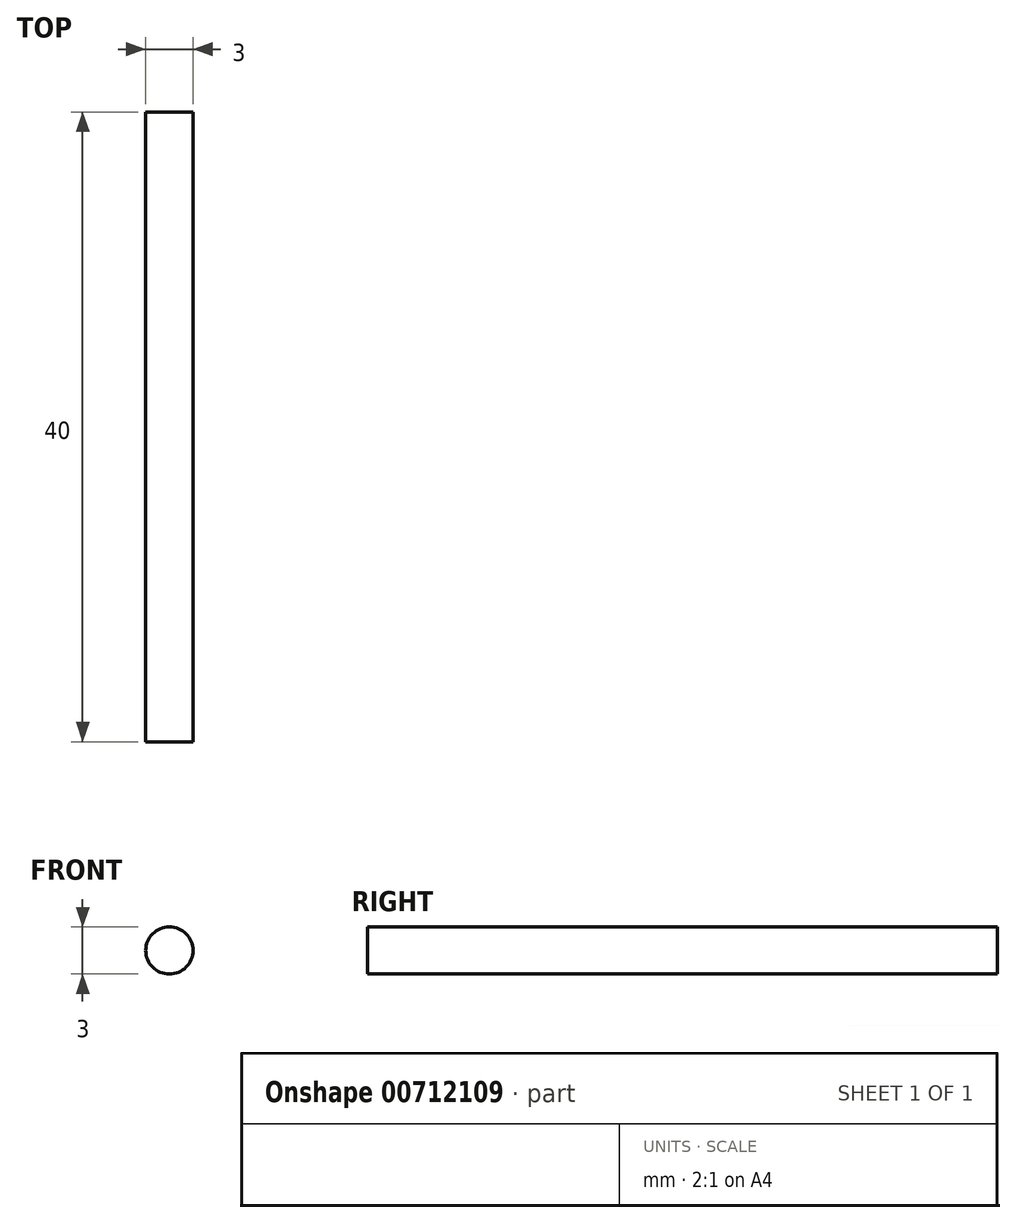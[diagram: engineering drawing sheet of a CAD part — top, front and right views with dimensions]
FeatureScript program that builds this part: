
annotation { "Feature Type Name" : "Feature", "Feature Type Description" : "" }
export const myFeature = defineFeature(function(context is Context, id is Id, definition is map)
    precondition{}
    {
        {
            var Q0;
            Q0=qCreatedBy(makeId("Front.planeOp"),FACE);
            var sketch = newSketch(context, id + "F0", { "sketchPlane" : qUnion([Q0])});
            skCircle(sketch, "E0", {"center": v(0, 0) * mm, "radius": 1.5 * mm});
            skSolve(sketch);
        }
        {
            var Q0;
            Q0 = qSketchRegion(id + "F0", true);
            extrude(context, id + "F1", {"entities" : qUnion([Q0]), "oppositeDirection" : true, "depth" : 40 * mm, "offsetDistance" : 25 * mm, "symmetric" : true});
        }
    });
